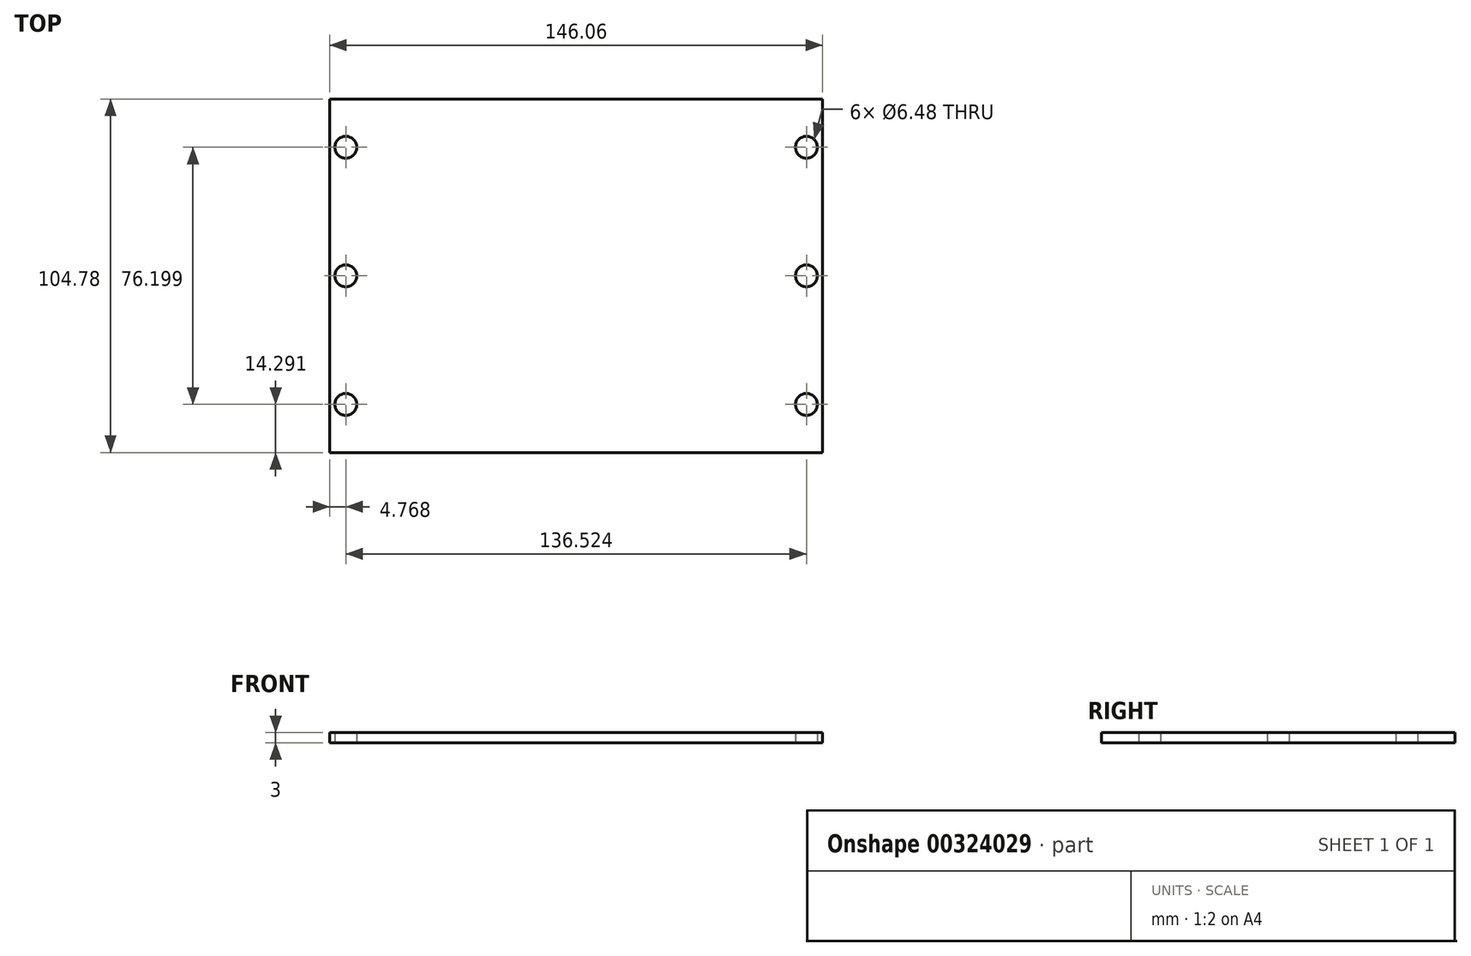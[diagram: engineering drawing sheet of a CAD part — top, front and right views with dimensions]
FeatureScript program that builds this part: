
annotation { "Feature Type Name" : "Feature", "Feature Type Description" : "" }
export const myFeature = defineFeature(function(context is Context, id is Id, definition is map)
    precondition{}
    {
        {
            var Q0;
            Q0=qCreatedBy(makeId("Top.planeOp"),FACE);
            var sketch = newSketch(context, id + "F0", { "sketchPlane" : qUnion([Q0])});
            skLineSegment(sketch, "E0", {"start": v(68.26, 31.75) * mm, "end": v(72.22, 31.75) * mm});
            skLineSegment(sketch, "E1", {"start": v(72.22, 6.35) * mm, "end": v(72.22, 31.75) * mm});
            skLineSegment(sketch, "E2", {"start": v(68.26, 6.35) * mm, "end": v(72.22, 6.35) * mm});
            skArc(sketch, "E3", {"start": v(68.26, 6.35) * mm, "mid": v(61.91, 0) * mm, "end": v(68.26, -6.35) * mm});
            skLineSegment(sketch, "E4", {"start": v(68.26, -6.35) * mm, "end": v(72.22, -6.35) * mm});
            skLineSegment(sketch, "E5", {"start": v(72.22, -31.75) * mm, "end": v(72.22, -6.35) * mm});
            skLineSegment(sketch, "E6", {"start": v(68.26, -31.75) * mm, "end": v(72.22, -31.75) * mm});
            skArc(sketch, "E7", {"start": v(68.26, -31.75) * mm, "mid": v(61.91, -38.1) * mm, "end": v(68.26, -44.45) * mm});
            skLineSegment(sketch, "E8", {"start": v(68.26, -44.45) * mm, "end": v(72.22, -44.45) * mm});
            skLineSegment(sketch, "E9", {"start": v(72.22, -51.59) * mm, "end": v(72.22, -44.45) * mm});
            skLineSegment(sketch, "E10", {"start": v(-72.23, -51.59) * mm, "end": v(72.23, -51.59) * mm});
            skLineSegment(sketch, "E11", {"start": v(-72.23, -51.59) * mm, "end": v(-72.23, -44.45) * mm});
            skLineSegment(sketch, "E12", {"start": v(-68.26, -44.45) * mm, "end": v(-72.23, -44.45) * mm});
            skArc(sketch, "E13", {"start": v(-68.26, -44.45) * mm, "mid": v(-61.91, -38.1) * mm, "end": v(-68.26, -31.75) * mm});
            skLineSegment(sketch, "E14", {"start": v(-68.26, -31.75) * mm, "end": v(-72.23, -31.75) * mm});
            skLineSegment(sketch, "E15", {"start": v(-72.23, -31.75) * mm, "end": v(-72.23, -6.35) * mm});
            skLineSegment(sketch, "E16", {"start": v(-68.26, -6.35) * mm, "end": v(-72.23, -6.35) * mm});
            skArc(sketch, "E17", {"start": v(-68.26, -6.35) * mm, "mid": v(-61.91, 0) * mm, "end": v(-68.26, 6.35) * mm});
            skLineSegment(sketch, "E18", {"start": v(-68.26, 6.35) * mm, "end": v(-72.23, 6.35) * mm});
            skLineSegment(sketch, "E19", {"start": v(-72.23, 6.35) * mm, "end": v(-72.23, 31.75) * mm});
            skLineSegment(sketch, "E20", {"start": v(-68.26, 31.75) * mm, "end": v(-72.23, 31.75) * mm});
            skArc(sketch, "E21", {"start": v(-68.26, 31.75) * mm, "mid": v(-61.91, 38.1) * mm, "end": v(-68.26, 44.45) * mm});
            skLineSegment(sketch, "E22", {"start": v(-68.26, 44.45) * mm, "end": v(-72.23, 44.45) * mm});
            skLineSegment(sketch, "E23", {"start": v(-72.23, 44.45) * mm, "end": v(-72.23, 51.59) * mm});
            skLineSegment(sketch, "E24", {"start": v(72.22, 51.59) * mm, "end": v(-72.23, 51.59) * mm});
            skLineSegment(sketch, "E25", {"start": v(72.22, 44.45) * mm, "end": v(72.22, 51.59) * mm});
            skLineSegment(sketch, "E26", {"start": v(68.26, 44.45) * mm, "end": v(72.22, 44.45) * mm});
            skArc(sketch, "E27", {"start": v(68.26, 44.45) * mm, "mid": v(61.91, 38.1) * mm, "end": v(68.26, 31.75) * mm});
            skCircle(sketch, "E28", {"center": v(-68.26, 0) * mm, "radius": 3.24 * mm});
            skCircle(sketch, "E29", {"center": v(-68.26, -38.1) * mm, "radius": 3.24 * mm});
            skCircle(sketch, "E30", {"center": v(68.26, 0) * mm, "radius": 3.24 * mm});
            skCircle(sketch, "E31", {"center": v(-68.26, 38.1) * mm, "radius": 3.24 * mm});
            skCircle(sketch, "E32", {"center": v(68.26, -38.1) * mm, "radius": 3.24 * mm});
            skCircle(sketch, "E33", {"center": v(68.26, 38.1) * mm, "radius": 3.24 * mm});
            skLineSegment(sketch, "E34", {"start": v(-73.03, -52.39) * mm, "end": v(-73.03, 52.39) * mm});
            skLineSegment(sketch, "E35", {"start": v(73.03, -52.39) * mm, "end": v(73.03, 52.39) * mm});
            skLineSegment(sketch, "E36", {"start": v(73.03, 52.39) * mm, "end": v(-73.03, 52.39) * mm});
            skLineSegment(sketch, "E37", {"start": v(-73.03, -52.39) * mm, "end": v(73.03, -52.39) * mm});
            skSolve(sketch);
        }
        {
            var Q0;
            Q0 = qSketchRegion(id + "F0", true);
            var Q1;
            Q1=makeQuery(id+"F0.imprint","IMPRINT",FACE,{"disambiguationData":[TD([[makeQuery(id+"F0.imprint","IMPRINT",EDGE,{"derivedFrom":sQuery(id+"F0.wireOp",EDGE,"E6")}),1.0]])]});
            extrude(context, id + "F1", {"entities" : qUnion([Q0, Q1]), "depth" : 3 * mm});
        }
    });
